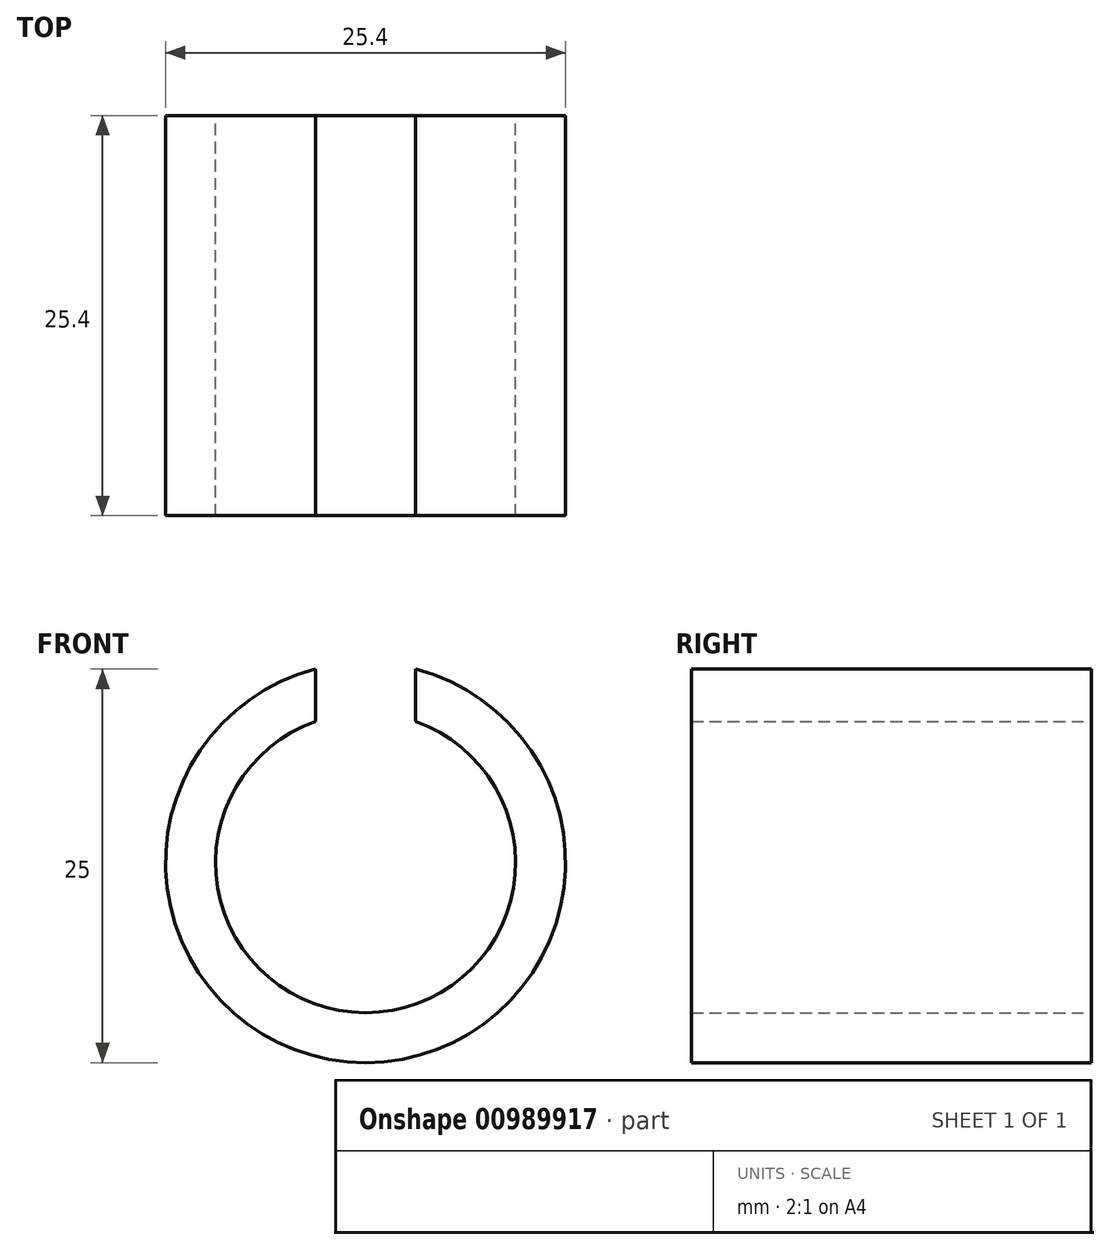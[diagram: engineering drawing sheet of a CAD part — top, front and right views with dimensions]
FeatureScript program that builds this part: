
annotation { "Feature Type Name" : "Feature", "Feature Type Description" : "" }
export const myFeature = defineFeature(function(context is Context, id is Id, definition is map)
    precondition{}
    {
        {
            var Q0;
            Q0=qCreatedBy(makeId("Front.planeOp"),FACE);
            var sketch = newSketch(context, id + "F0", { "sketchPlane" : qUnion([Q0])});
            skArc(sketch, "E0", {"start": v(-3.18, 8.98) * mm, "mid": v(0, -9.53) * mm, "end": v(3.17, 8.98) * mm});
            skArc(sketch, "E1", {"start": v(-3.18, 12.3) * mm, "mid": v(0, -12.7) * mm, "end": v(3.18, 12.3) * mm});
            skLineSegment(sketch, "E2.left", {"start": v(-3.18, 8.98) * mm, "end": v(-3.18, 12.3) * mm});
            skLineSegment(sketch, "E2.right", {"start": v(3.18, 8.98) * mm, "end": v(3.18, 12.3) * mm});
            skSolve(sketch);
        }
        {
            var Q0;
            Q0=makeQuery(id+"F0.imprint","IMPRINT",FACE,{"disambiguationData":[TD([[makeQuery(id+"F0.imprint","IMPRINT",EDGE,{"derivedFrom":sQuery(id+"F0.wireOp",EDGE,"E0")}),-1.0]])]});
            extrude(context, id + "F1", {"entities" : qUnion([Q0]), "endBound" : BoundingType.SYMMETRIC, "depth" : 25.4 * mm, "offsetDistance" : 25.4 * mm});
        }
    });
